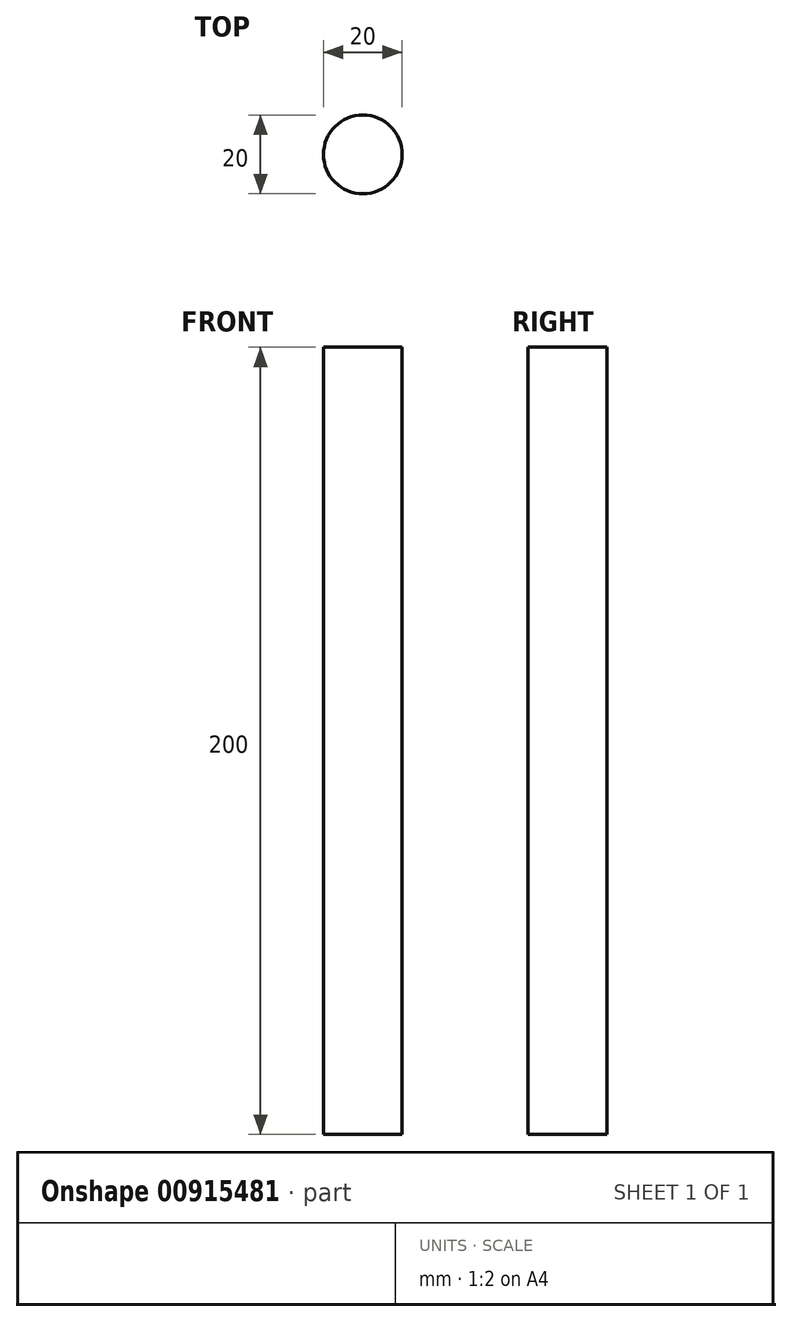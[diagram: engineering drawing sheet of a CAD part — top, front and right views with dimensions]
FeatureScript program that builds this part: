
annotation { "Feature Type Name" : "Feature", "Feature Type Description" : "" }
export const myFeature = defineFeature(function(context is Context, id is Id, definition is map)
    precondition{}
    {
        {
            var Q0;
            Q0=qCreatedBy(makeId("Top.planeOp"),FACE);
            var sketch = newSketch(context, id + "F0", { "sketchPlane" : qUnion([Q0])});
            skCircle(sketch, "E0", {"center": v(0, 0) * mm, "radius": 10 * mm});
            skSolve(sketch);
        }
        {
            var Q0;
            Q0=makeQuery(id+"F0.imprint","IMPRINT",FACE,{"disambiguationData":[TD([[makeQuery(id+"F0.imprint","IMPRINT",EDGE,{"derivedFrom":sQuery(id+"F0.wireOp",EDGE,"E0")}),1.0]])]});
            extrude(context, id + "F1", {"entities" : qUnion([Q0]), "depth" : 200 * mm, "offsetDistance" : 25 * mm});
        }
    });
